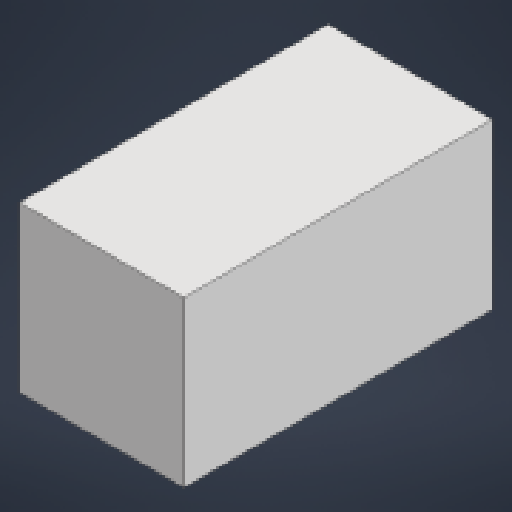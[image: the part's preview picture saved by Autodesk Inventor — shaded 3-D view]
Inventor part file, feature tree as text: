
AUTODESK INVENTOR PART (.ipt)
format: ipt  version: 2023 (Build 270158000, 158)  size: 97,280 bytes
history: native  units: in
note: dims shown in document units (in); Inventor stores cm internally (conversion verified against a paired STEP export)
features: extrude x1, sketch x1
ambient origin geometry x8: Origin, YZ Plane, XZ Plane, XY Plane, X Axis, Y Axis, Z Axis, Center Point
bodies: Solid1 (feature_tree)
feature tree (2):
  extrude  "Extrusion1"  Depth=3.0in
  sketch  "Sketch1"  dims[d0=1.6in d1=3.0in d2=1.6in d3=0.0in]
